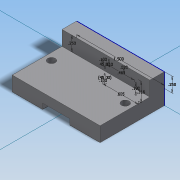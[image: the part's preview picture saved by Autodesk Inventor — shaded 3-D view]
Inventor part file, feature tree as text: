
AUTODESK INVENTOR PART (.ipt)
format: ipt  version: 2014 SP2 (Build 180246200, 246)  size: 137,728 bytes
history: native  units: in
note: dims shown in document units (in); Inventor stores cm internally (conversion verified against a paired STEP export)
features: extrude x5, sketch x2, other x1, hole x1, mirror x1
ambient origin geometry x8: Origin, YZ Plane, XZ Plane, XY Plane, X Axis, Y Axis, Z Axis, Center Point
bodies: Solid1 (feature_tree)
feature tree (10):
  other  "XT60"
  sketch  "Sketch2"  dims[d0=0.605in d1=0.316in]
  extrude  "Extrusion1"  Depth=0.316in
  extrude  "Extrusion2"  TaperAngle=45.0deg  [1 undecoded]
  extrude  "Extrusion3"  Depth=0.25in
  hole  "Hole1"  [1 undecoded]
  mirror  "Mirror1"
  extrude  "Extrusion4"  Depth=0.25in
  extrude  "Extrusion5"  Depth=0.25in
  sketch  "Sketch3"  dims[d2=0.1in d3=45.0deg d4=0.1in d5=45.0deg d6=0.01in d7=0.02in d8=1.5in d9=0.25in d10=1.1in d11=0.0in d12=0.724in d13=0.0in d14=0.418in d15=0.0in d16=0.63in d17=0.55in d18=0.129in d19=0.75in d20=0.225in d21=0.25in d22=0.5635in d23=1.0in d24=0.8108in d25=0.465in d26=0.19in d27=0.0in d28=0.0in d29=0.25in d30=0.25in d31=0.0in]
note: 2 required parameter values undecoded (feature->parameter linkage not recoverable at this tier; creation-order binding heuristic only, values carry confidence <= 0.55)
